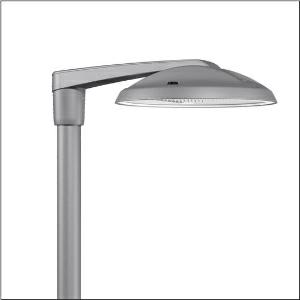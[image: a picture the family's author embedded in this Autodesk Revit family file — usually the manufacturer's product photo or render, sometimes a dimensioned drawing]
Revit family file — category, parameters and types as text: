
# Revit family: dl_r__50_iq_mini___st1_0a_5xa248d31v08ne_16c2
name_source: partatom
category: Lighting Fixtures
units: mm (PartAtom-declared; Revit-internal decimal feet)

## family parameters
Cut with Voids When Loaded = No
Host = Face
Light Source = No
Part Type = Normal
Room Calculation Point = No
Round Connector Dimension = Use Diameter
Shared = No

## types (1)
- --- (1 x LED, 17900 lm, 110.1 W, 3000K)
    Apparent Load = 110 VA
    CIE Flux Codes = 37 72 97 100 100
    Color Rendering = 70
    Color Temperature = 3000K
    Default Elevation = 1800 mm
    Description = DL® 50 iQ mini, mast luminaire, primary light control with lens, of PMMA, primary optical cover: cover, of toughened safety glass, transparent, light distribution: ST1.0a, light emission: direct distribution, primary light characteristic: asymmetric, installation type: post-top, side-entry, LED, High Power LED, rated luminous flux: 17.900lm, luminous efficacy: 163lm/W, light colour: 730, colour temperature: 3000K, control: optimised constant luminous flux control (CLO 2.0), Desk-Remote (wireless, voltage-free reading and setting of iQ features in the workshop via application-optimized NFC function/RFID function), Light-Fading, Smart-Wire, Night-Set, Lumen-Switch, Temp-Guard, Auto-Match, Street-Remote, presetting dimming logarithmic, mains connection: 230..240V, AC, 50/60Hz, connection cable pre-assembled, cable length: 10,5m, start of lifetime: 110W, end of service life: 116W, reduction: 50W, luminaire housing, of diecast aluminium, powder-coated, Siteco® metallic grey (DB 702S), inclination adjustable: 0°, 5°, 10° (post-top) | 0°, -5°, -10°, -15° (side-entry), please order mast post-top element or mast side-entry element separately, diameter: 500mm, height: 115mm, post-top: for spigot size d x l = 76 x 100mm; with reducer (optional accessory) 60 x 100mm | side-entry: for spigot size d x l = 60 x 100mm; with reducer (optional accessory) 42 x 100mm, Smart Interface above, protection rating (complete): IP66, insulation class (complete): insulation class II (safety insulation), certification: CE, ENEC, VDE, impact resistance: IK08, permissible operating ambient temperature for outdoor applications: -25..+40°C, standard-compliant lighting for roads and squares, packaging unit: 1 piece

Light Distribution: ST1.0a
    Height = 115 mm
    Lamp = 1 x LED
    Lamp Light Flux = 17900 lm
    Lamp Power = 110.1 W
    Lamp count = 1
    Length = 500 mm
    Luminous efficacy = 163 lm/W
    Manufacturer = Siteco
    ModVariant = No
    Model = 5XA248D31V08NE
    Number of Poles = 1
    OnlyDefault = Yes
    Power Factor = 1
    Product Name = DL® 50 iQ mini | ST1.0a
    Product group = mast luminaire | pylon top
    ProductGroupID = 6100
    Protection Class = Protection class II
    Protection Degree = IP 66
    RLX_Detail_Level = 1
    RLX_Emergency_Light_Flux = 0 lm
    RLX_Emergency_Type = 0
    RLX_Emergency_Type_DB = No
    RlxData = <blob elided: 106317 chars, md5=07c96c00>
    Socket = socket
    Standby Power = 0 W
    System Light Flux = 17900 lm
    System Power = 110 W
    Type Comments = factory setting: luminous flux: 100 % | dim-lin: 254 | 601 mA
    Type Image = l_1251788.jpg
    URL = http://relux.com
    VarID = @adj_024069
    Voltage = 0 V
    Weight = 0.00 kg
    Width = 0 mm  [stored 0 ft]

note: [stored X ft] marks values corroborated as IEEE doubles in the binary element streams (Revit-internal decimal feet)

## geometry (parser evidence)
native form markers: Blend x4, Sweep x11
no freeform markers — native parametric forms only
